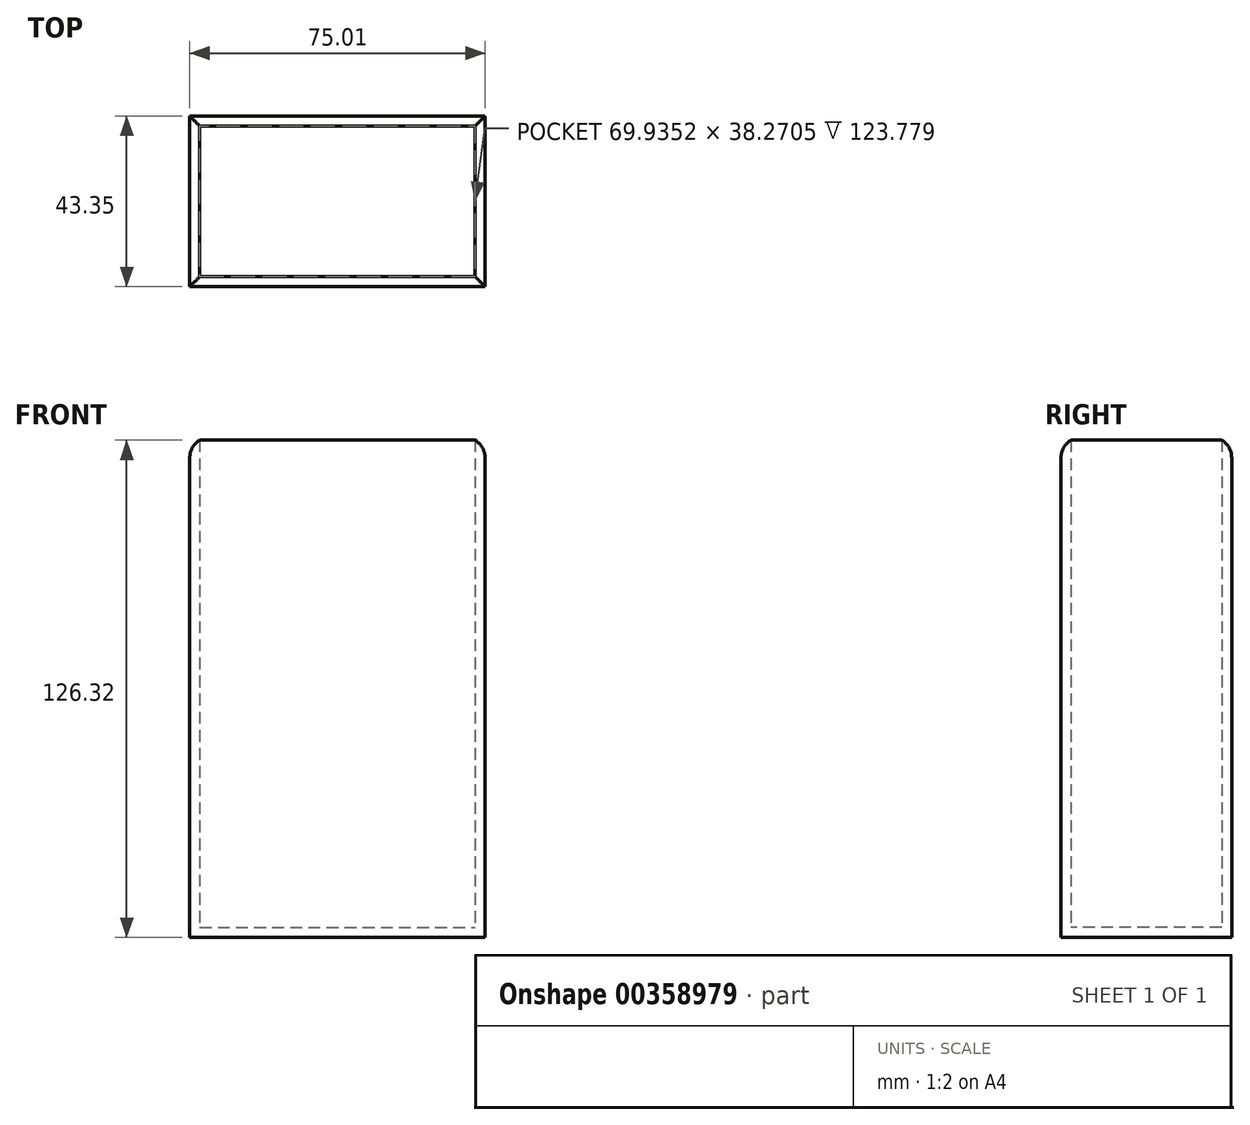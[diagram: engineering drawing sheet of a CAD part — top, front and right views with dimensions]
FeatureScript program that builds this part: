
annotation { "Feature Type Name" : "Feature", "Feature Type Description" : "" }
export const myFeature = defineFeature(function(context is Context, id is Id, definition is map)
    precondition{}
    {
        {
            var Q0;
            Q0=qCreatedBy(makeId("Top.planeOp"),FACE);
            var sketch = newSketch(context, id + "F0", { "sketchPlane" : qUnion([Q0])});
            skLineSegment(sketch, "E0.bottom", {"start": v(-35.62, 22.33) * mm, "end": v(39.4, 22.33) * mm});
            skLineSegment(sketch, "E0.top", {"start": v(-35.62, -21.02) * mm, "end": v(39.4, -21.02) * mm});
            skLineSegment(sketch, "E0.left", {"start": v(-35.62, 22.33) * mm, "end": v(-35.62, -21.02) * mm});
            skLineSegment(sketch, "E0.right", {"start": v(39.4, 22.33) * mm, "end": v(39.4, -21.02) * mm});
            skSolve(sketch);
        }
        {
            var Q0;
            Q0=makeQuery(id+"F0.imprint","IMPRINT",FACE,{"disambiguationData":[TD([[makeQuery(id+"F0.imprint","IMPRINT",EDGE,{"derivedFrom":sQuery(id+"F0.wireOp",EDGE,"E0.bottom")}),-1.0]])]});
            extrude(context, id + "F1", {"entities" : qUnion([Q0]), "depth" : 127 * mm});
        }
        {
            var Q0;
            Q0=makeQuery(id+"F1.opExtrude","CAP_FACE",FACE,{"disambiguationData":[OSD([sQuery(id+"F0.wireOp",EDGE,"E0.bottom"),sQuery(id+"F0.wireOp",EDGE,"E0.top"),sQuery(id+"F0.wireOp",EDGE,"E0.left"),sQuery(id+"F0.wireOp",EDGE,"E0.right")])],"isStart":false});
            shell(context, id + "F2", {"entities" : qUnion([Q0]), "thickness" : 2.54 * mm});
        }
        {
            var Q0;
            Q0=makeQuery(id+"F1.opExtrude","CAP_EDGE",EDGE,{"disambiguationData":[OSD([sQuery(id+"F0.wireOp",EDGE,"E0.bottom")])],"isStart":false});
            var Q1;
            Q1=makeQuery(id+"F1.opExtrude","CAP_EDGE",EDGE,{"disambiguationData":[OSD([sQuery(id+"F0.wireOp",EDGE,"E0.left")])],"isStart":false});
            var Q2;
            Q2=makeQuery(id+"F1.opExtrude","CAP_EDGE",EDGE,{"disambiguationData":[OSD([sQuery(id+"F0.wireOp",EDGE,"E0.top")])],"isStart":false});
            var Q3;
            Q3=makeQuery(id+"F1.opExtrude","CAP_EDGE",EDGE,{"disambiguationData":[OSD([sQuery(id+"F0.wireOp",EDGE,"E0.right")])],"isStart":false});
            fillet(context, id + "F3", {"entities" : qUnion([Q0, Q1, Q2, Q3]), "radius" : 5.08 * mm, "tangentPropagation" : true, "allowEdgeOverflow" : false});
        }
        {
            var Q0;
            Q0=makeQuery(id+"F2.opShell","OFFSET_FACE",FACE,{"disambiguationData":[OSD([sQuery(id+"F0.wireOp",EDGE,"E0.bottom"),sQuery(id+"F0.wireOp",EDGE,"E0.top"),sQuery(id+"F0.wireOp",EDGE,"E0.left"),sQuery(id+"F0.wireOp",EDGE,"E0.right")])]});
            cPlane(context, id + "F4", {"entities" : qUnion([Q0]), "cplaneType" : CPlaneType.OFFSET, "offset" : 166.88 * mm, "width" : 152.4 * mm, "height" : 152.4 * mm});
        }
    });
